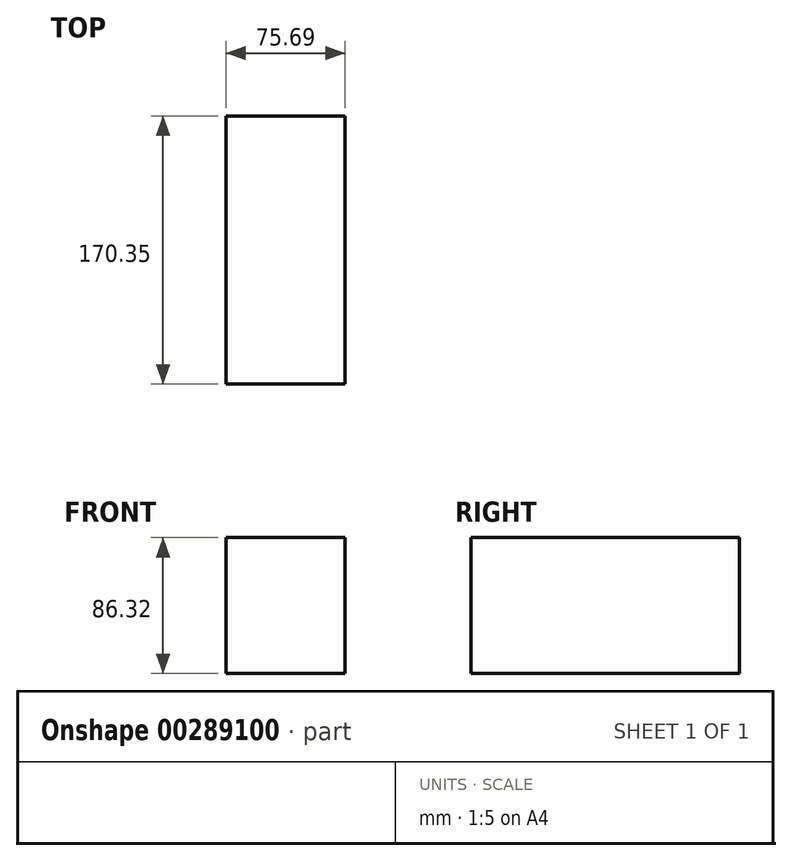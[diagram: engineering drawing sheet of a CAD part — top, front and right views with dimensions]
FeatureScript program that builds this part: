
annotation { "Feature Type Name" : "Feature", "Feature Type Description" : "" }
export const myFeature = defineFeature(function(context is Context, id is Id, definition is map)
    precondition{}
    {
        {
            var Q0;
            Q0=qCreatedBy(makeId("Right.planeOp"),FACE);
            var sketch = newSketch(context, id + "F0", { "sketchPlane" : qUnion([Q0])});
            skLineSegment(sketch, "E0.bottom", {"start": v(-80.77, 37.4) * mm, "end": v(89.58, 37.4) * mm});
            skLineSegment(sketch, "E0.top", {"start": v(-80.77, -48.91) * mm, "end": v(89.58, -48.91) * mm});
            skLineSegment(sketch, "E0.left", {"start": v(-80.77, 37.4) * mm, "end": v(-80.77, -48.91) * mm});
            skLineSegment(sketch, "E0.right", {"start": v(89.58, 37.4) * mm, "end": v(89.58, -48.91) * mm});
            skSolve(sketch);
        }
        {
            var Q0;
            Q0=makeQuery(id+"F0.imprint","IMPRINT",FACE,{"disambiguationData":[TD([[makeQuery(id+"F0.imprint","IMPRINT",EDGE,{"derivedFrom":sQuery(id+"F0.wireOp",EDGE,"E0.bottom")}),-1.0]])]});
            extrude(context, id + "F1", {"entities" : qUnion([Q0]), "depth" : 75.7 * mm});
        }
    });
